# Revit family: PRD_FrankeWS_UrnlDvdrs_CampusUrinalDivider_CMPX700
name_source: partatom
category: Furniture
revit_build: Autodesk Revit 2018 (Build: 20190510_1515(x64)
units: mm (PartAtom-declared; Revit-internal decimal feet)

## family parameters
Cut with Voids When Loaded = No
Host = Face
OmniClass Number = 23.40.20.21
OmniClass Title = Toilet and Bath Specialties
Room Calculation Point = No
Shared = No

## types (1)
- CMPX700
    AssetType = Fixed
    BIMObjectName = PRD_AR_UrinalDividers_CampusUrinalDivider_CMPX700
    Category = Pr_40_20_93_74, Urinal dividers
    Color = Stainless steel
    Default Elevation = 1200 mm
    Description = Urinal divider for wall mounting, stainless steel, surface satin finished with WL5 1 mm structure, material thickness 2 mm, hidden wall mounting, included screws and dowels.
    DividerMaterial = PRD_AR_StainlessSteel_SatinFinished
    DurationUnit = year
    Features = stainless steel, 2.00 mm, textured, wall mounting, 60x740x440 mm (WxHxD)
    Finish = Satin finished
    IfcExportAs = IfcFurnitureType
    IfcExportType = NOTDEFINED
    MainColor = Stainless steel
    Manufacturer = KWC Group AG
    ManufacturerName = KWC Group AG
    ManufacturerURL = www.kwc.com
    Material = Stainless steel
    MaterialFinish = Satin finished
    MaterialsBody = Stainless steel 1.4301
    Model = CMPX700
    ModelNumber = 2000056977
    ModelReference = CMPX700
    NBSDescription = Urinal divider
    NBSReference = 45-35-70/358
    Name = CAMPUS urinal divider CMPX700
    NominalDepth = 440 mm  [stored 1.44357 ft]
    NominalHeight = 740 mm  [stored 2.42782 ft]
    NominalLength = 60 mm  [stored 0.19685 ft]
    NominalWidth = 60 mm  [stored 0.19685 ft]
    ProductInformation = https://pim.kwc.com
    Size = 60 x 740 x 440 mm
    Style = Urinal divider
    TypeOfMounting = Wall mounting
    URL = www.kwc.com
    Uniclass2015Code = Pr_40_20_93_74
    Uniclass2015Title = Urinal divider
    Uniclass2015Version = Products v1.5
    Version = 1
    WarrantyDurationUnit = year

note: [stored X ft] marks values corroborated as IEEE doubles in the binary element streams (Revit-internal decimal feet)

## geometry (parser evidence)
native form markers: Sweep x1
no freeform markers — native parametric forms only
